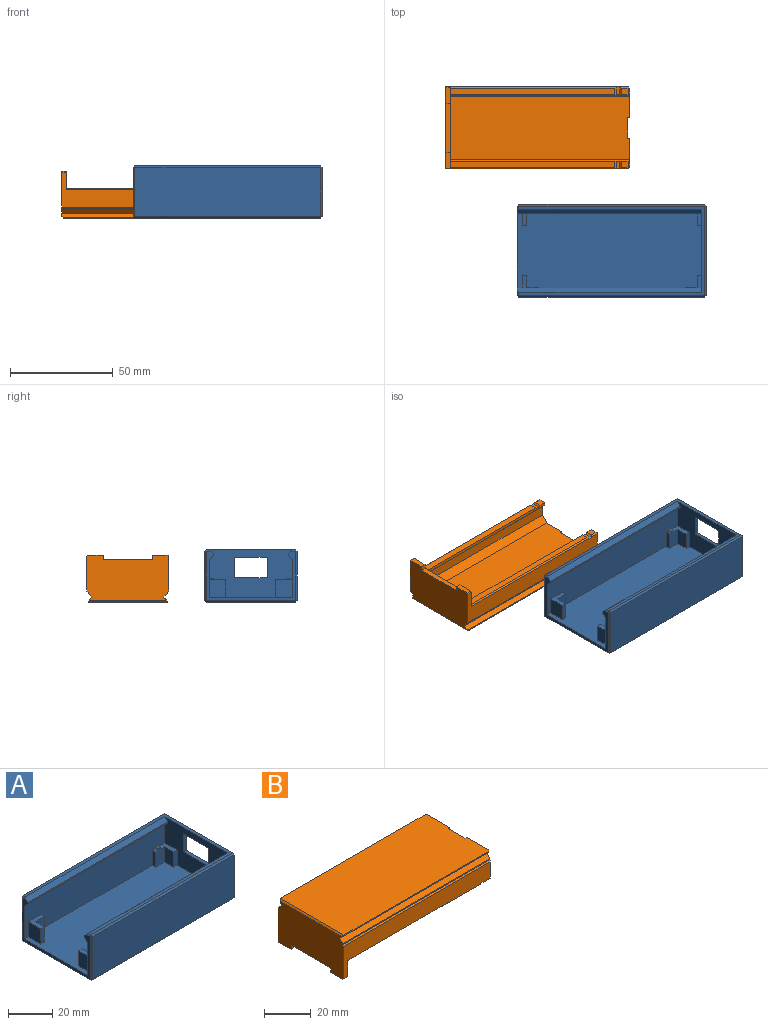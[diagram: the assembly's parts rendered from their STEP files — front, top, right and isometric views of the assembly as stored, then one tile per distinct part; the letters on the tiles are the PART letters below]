
ASSEMBLY  parts=2 mates=1
PART A: 75 faces, bbox 92.1x45.1x25.4 mm
  f0: plane 8x4mm, normal (0,0,1), area 21.6mm2, adj f1,f4,f29,f30,f32,f72
  f1: plane 89.7x18.2mm, normal (0,1,0), area 1496.4mm2, adj f0,f4,f6,f8,f15,f16,f17,f31
  f2: plane 2.2x1.08mm, normal (0,0,1), area 2.4mm2, adj f3,f24,f27,f70
  f3: plane 89.7x18.2mm, normal (0,-1,0), area 1496.4mm2, adj f2,f4,f6,f8,f18,f19,f23,f27
  f4: plane 40.3x23mm, normal (-1,0,0), area 621.3mm2, adj f0,f1,f3,f6,f11,f26,f28,f32
  f5: plane 43.5x23.8mm, normal (1,0,0), area 831.1mm2, adj f49,f50,f57,f58,f65,f66,f67,f68
  f6: plane 89.7x40.3mm, normal (0,0,1), area 3493.5mm2, adj f1,f3,f4,f8,f12,f13,f14,f15
  f7: plane 90.5x23.8mm, normal (0,1,0), area 2153.9mm2, adj f56,f57,f61,f62
  f8: plane 43.5x23.8mm, normal (-1,0,0), area 151.2mm2, adj f1,f3,f6,f34,f35,f36,f37,f38
  f9: plane 90.5x23.8mm, normal (0,-1,0), area 2153.9mm2, adj f47,f48,f50,f51
  f10: plane 90.5x43.5mm, normal (0,0,-1), area 3936.7mm2, adj f48,f49,f55,f56
  f11: plane 90.5x43.5mm, normal (0,0,1), area 354.1mm2, adj f4,f36,f37,f45,f51,f58,f62,f64
  f12: plane 8.4x5.8mm, normal (0,1,0), area 48.7mm2, adj f6,f13,f16,f17
  f13: plane 8.4x5.8mm, normal (1,0,0), area 48.7mm2, adj f6,f12,f14,f17
  f14: plane 8.4x2.2mm, normal (0,1,0), area 18.5mm2, adj f6,f13,f15,f17
  f15: plane 8.4x8mm, normal (-1,0,0), area 67.2mm2, adj f1,f6,f14,f17
  f16: plane 8.4x2.2mm, normal (1,0,0), area 18.5mm2, adj f1,f6,f12,f17
  f17: plane 8x8mm, normal (0,0,1), area 30.4mm2, adj f1,f12,f13,f14,f15,f16
  f18: plane 8.4x2.2mm, normal (1,0,0), area 18.5mm2, adj f3,f6,f22,f23
  f19: plane 8.4x8mm, normal (-1,0,0), area 67.2mm2, adj f3,f6,f20,f23
  f20: plane 8.4x2.2mm, normal (0,-1,0), area 18.5mm2, adj f6,f19,f21,f23
  f21: plane 8.4x5.8mm, normal (1,0,0), area 48.7mm2, adj f6,f20,f22,f23
  f22: plane 8.4x5.8mm, normal (0,-1,0), area 48.7mm2, adj f6,f18,f21,f23
  f23: plane 8x8mm, normal (0,0,1), area 30.4mm2, adj f3,f18,f19,f20,f21,f22
  f24: plane 9.2x5.8mm, normal (0,-1,0), area 50.4mm2, adj f2,f6,f25,f27,f28,f69,f70,f71
  f25: plane 8.4x5.8mm, normal (-1,0,0), area 48.7mm2, adj f6,f24,f26,f28
  f26: plane 8.4x2.2mm, normal (0,-1,0), area 18.5mm2, adj f4,f6,f25,f28
  f27: plane 8.4x2.2mm, normal (-1,0,0), area 18.5mm2, adj f2,f3,f6,f24
  f28: plane 8x4mm, normal (0,0,1), area 21.6mm2, adj f3,f4,f24,f25,f26,f71
  f29: plane 8.4x5.8mm, normal (-1,0,0), area 48.7mm2, adj f0,f6,f30,f32
  f30: plane 9.2x5.8mm, normal (0,1,0), area 50.4mm2, adj f0,f6,f29,f31,f33,f72,f73,f74
  f31: plane 8.4x2.2mm, normal (-1,0,0), area 18.5mm2, adj f1,f6,f30,f33
  f32: plane 8.4x2.2mm, normal (0,1,0), area 18.5mm2, adj f0,f4,f6,f29
  f33: plane 2.2x1.08mm, normal (0,0,1), area 2.4mm2, adj f1,f30,f31,f74
  f34: plane 89.7x0.8mm, normal (0,-1,0), area 71.8mm2, adj f4,f8,f35,f36
  f35: plane 89.7x2mm, normal (0,-0.71,-0.71), area 253.7mm2, adj f3,f4,f8,f34
  f36: plane 89.7x2mm, normal (0,-0.71,0.71), area 253.3mm2, adj f4,f8,f11,f34,f64
  f37: plane 89.7x2mm, normal (0,0.71,0.71), area 253.3mm2, adj f4,f8,f11,f38,f45
  f38: plane 89.7x0.8mm, normal (0,1,0), area 71.8mm2, adj f4,f8,f37,f39
  f39: plane 89.7x2mm, normal (0,0.71,-0.71), area 253.7mm2, adj f1,f4,f8,f38
  f40: plane 16x1.6mm, normal (0,0,-1), area 25.6mm2, adj f4,f41,f43,f66
  f41: plane 10x1.6mm, normal (0,1,0), area 16mm2, adj f4,f40,f42,f65
  f42: plane 16x1.6mm, normal (0,0,1), area 25.6mm2, adj f4,f41,f43,f67
  f43: plane 10x1.6mm, normal (0,-1,0), area 16mm2, adj f4,f40,f42,f68
  f44: plane 0.8x0.8mm, normal (0.58,-0.58,-0.58), area 0.6mm2, adj f48,f49,f50
  f45: plane 2.4x0.8mm, normal (-0.71,0,0.71), area 2.3mm2, adj f8,f11,f37,f46
  f46: plane 0.8x0.8mm, normal (-0.58,-0.58,0.58), area 0.6mm2, adj f45,f47,f51
  f47: plane 23.8x0.8mm, normal (-0.71,-0.71,0), area 26.9mm2, adj f8,f9,f46,f52
  f48: plane 90.5x0.8mm, normal (0,-0.71,-0.71), area 102.4mm2, adj f9,f10,f44,f52
  f49: plane 43.5x0.8mm, normal (0.71,0,-0.71), area 49.2mm2, adj f5,f10,f44,f53
  f50: plane 23.8x0.8mm, normal (0.71,-0.71,0), area 26.9mm2, adj f5,f9,f44,f54
  f51: plane 90.5x0.8mm, normal (0,-0.71,0.71), area 102.4mm2, adj f9,f11,f46,f54
  f52: plane 0.8x0.8mm, normal (-0.58,-0.58,-0.58), area 0.6mm2, adj f47,f48,f55
  f53: plane 0.8x0.8mm, normal (0.58,0.58,-0.58), area 0.6mm2, adj f49,f56,f57
  f54: plane 0.8x0.8mm, normal (0.58,-0.58,0.58), area 0.6mm2, adj f50,f51,f58
  f55: plane 43.5x0.8mm, normal (-0.71,0,-0.71), area 49.2mm2, adj f8,f10,f52,f59
  f56: plane 90.5x0.8mm, normal (0,0.71,-0.71), area 102.4mm2, adj f7,f10,f53,f59
  f57: plane 23.8x0.8mm, normal (0.71,0.71,0), area 26.9mm2, adj f5,f7,f53,f60
  f58: plane 43.5x0.8mm, normal (0.71,0,0.71), area 49.2mm2, adj f5,f11,f54,f60
  f59: plane 0.8x0.8mm, normal (-0.58,0.58,-0.58), area 0.6mm2, adj f55,f56,f61
  f60: plane 0.8x0.8mm, normal (0.58,0.58,0.58), area 0.6mm2, adj f57,f58,f62
  f61: plane 23.8x0.8mm, normal (-0.71,0.71,0), area 26.9mm2, adj f7,f8,f59,f63
  f62: plane 90.5x0.8mm, normal (0,0.71,0.71), area 102.4mm2, adj f7,f11,f60,f63
  f63: plane 0.8x0.8mm, normal (-0.58,0.58,0.58), area 0.6mm2, adj f61,f62,f64
  f64: plane 2.4x0.8mm, normal (-0.71,0,0.71), area 2.3mm2, adj f8,f11,f36,f63
  f65: plane 11.6x0.8mm, normal (0.71,0.71,0), area 12.2mm2, adj f5,f41,f66,f67
  f66: plane 17.6x0.8mm, normal (0.71,0,-0.71), area 19mm2, adj f5,f40,f65,f68
  f67: plane 17.6x0.8mm, normal (0.71,0,0.71), area 19mm2, adj f5,f42,f65,f68
  f68: plane 11.6x0.8mm, normal (0.71,-0.71,0), area 12.2mm2, adj f5,f43,f66,f67
  f69: plane 2.2x1.32mm, normal (0,0,1), area 2.9mm2, adj f3,f24,f70,f71
  f70: plane 2.2x0.8mm, normal (-0.71,0,0.71), area 2.5mm2, adj f2,f3,f24,f69
  f71: plane 2.2x0.8mm, normal (0.71,0,0.71), area 2.5mm2, adj f3,f24,f28,f69
  f72: plane 2.2x0.8mm, normal (0.71,0,0.71), area 2.5mm2, adj f0,f1,f30,f73
  f73: plane 2.2x1.32mm, normal (0,0,1), area 2.9mm2, adj f1,f30,f72,f74
  f74: plane 2.2x0.8mm, normal (-0.71,0,0.71), area 2.5mm2, adj f1,f30,f33,f73
PART B: 63 faces, bbox 89.6x39.9x22.8 mm
  f0: plane 80x3.2mm, normal (0,0,-1), area 256mm2, adj f3,f7,f13,f57
  f1: plane 3.2x3.2mm, normal (0,0,-1), area 10.2mm2, adj f4,f6,f41,f62
  f2: plane 89x17mm, normal (0,1,0), area 785.2mm2, adj f7,f8,f9,f13,f42,f43,f45,f52
  f3: plane 86.4x1.6mm, normal (0,-1,0), area 136.3mm2, adj f0,f13,f29,f30,f44,f57,f58,f59
  f4: plane 86.4x1.6mm, normal (0,1,0), area 136.3mm2, adj f1,f13,f31,f32,f39,f60,f61,f62
  f5: plane 80.6x0.6mm, normal (0,-0.71,-0.71), area 68.1mm2, adj f13,f26,f31,f60
  f6: plane 3.8x0.6mm, normal (0,-0.71,-0.71), area 3mm2, adj f1,f26,f40,f62
  f7: plane 80.6x0.6mm, normal (0,0.71,-0.71), area 68.1mm2, adj f0,f2,f13,f57
  f8: plane 3.8x0.6mm, normal (0,0.71,-0.71), area 3mm2, adj f2,f30,f45,f58
  f9: plane 39.9x22mm, normal (-1,0,0), area 812.4mm2, adj f2,f10,f14,f15,f19,f20,f21,f24
  f10: plane 7.55x2.4mm, normal (0,0,-1), area 18.1mm2, adj f9,f13,f51,f55
  f11: plane 87.2x30.7mm, normal (0,0,-1), area 2667mm2, adj f12,f13,f22,f23,f25,f34,f35,f36
  f12: plane 14.35x13.8mm, normal (1,0,0), area 48.2mm2, adj f11,f17,f19,f20,f21,f22,f32,f33
  f13: plane 39.9x20.4mm, normal (1,0,0), area 703.5mm2, adj f0,f2,f3,f4,f5,f7,f10,f11
  f14: plane 89.6x1.88mm, normal (0,0.71,0.71), area 238.6mm2, adj f9,f15,f24,f25
  f15: plane 89.6x1.88mm, normal (0,0.71,-0.71), area 237.7mm2, adj f9,f14,f16,f25,f47,f49
  f16: plane 88x0.52mm, normal (0,1,0), area 45.5mm2, adj f15,f17,f47,f49
  f17: plane 88.8x38.7mm, normal (0,0,1), area 3425.9mm2, adj f12,f16,f18,f25,f34,f35,f36,f49
  f18: plane 88x0.52mm, normal (0,-1,0), area 45.5mm2, adj f17,f19,f48,f50
  f19: plane 89.6x1.88mm, normal (0,-0.71,-0.71), area 237.7mm2, adj f9,f12,f18,f20,f48,f50
  f20: plane 89.6x1.88mm, normal (0,-0.71,0.71), area 238.6mm2, adj f9,f12,f19,f21
  f21: plane 89.6x0.52mm, normal (0,-1,0), area 46.3mm2, adj f9,f12,f20,f37
  f22: plane 87.2x3.2mm, normal (0,0.71,-0.71), area 394.6mm2, adj f11,f12,f13,f33
  f23: plane 87.2x3.2mm, normal (0,-0.71,-0.71), area 394.6mm2, adj f11,f13,f25,f28
  f24: plane 89.6x0.52mm, normal (0,1,0), area 46.3mm2, adj f9,f14,f25,f42
  f25: plane 14.35x13.8mm, normal (1,0,0), area 48.2mm2, adj f11,f14,f15,f17,f23,f24,f28,f29
  f26: plane 89x17mm, normal (0,-1,0), area 785.2mm2, adj f5,f6,f9,f13,f37,f38,f40,f51
  f27: plane 7.55x2.4mm, normal (0,0,-1), area 18.1mm2, adj f9,f13,f52,f53
  f28: plane 87.2x5mm, normal (0,-1,0), area 436mm2, adj f13,f23,f25,f29
  f29: plane 87.2x2.4mm, normal (0,-0.71,0.71), area 295.5mm2, adj f3,f13,f25,f28,f44
  f30: plane 3.2x3.2mm, normal (0,0,-1), area 10.2mm2, adj f3,f8,f46,f58
  f31: plane 80x3.2mm, normal (0,0,-1), area 256mm2, adj f4,f5,f13,f60
  f32: plane 87.2x2.4mm, normal (0,0.71,0.71), area 295.5mm2, adj f4,f12,f13,f33,f39
  f33: plane 87.2x5mm, normal (0,1,0), area 436mm2, adj f12,f13,f22,f32
  f34: plane 2.4x1mm, normal (0,-1,0), area 2.4mm2, adj f11,f17,f25,f35
  f35: plane 10x2.4mm, normal (1,0,0), area 24mm2, adj f11,f17,f34,f36
  f36: plane 2.4x1mm, normal (0,1,0), area 2.4mm2, adj f11,f12,f17,f35
  f37: plane 89.6x0.6mm, normal (0,-0.71,0.71), area 75.8mm2, adj f9,f21,f26,f38
  f38: plane 9x0.6mm, normal (0.71,-0.71,0), area 7.4mm2, adj f12,f26,f37,f40
  f39: plane 2.4x0.8mm, normal (0.71,0.71,0), area 1.8mm2, adj f4,f12,f32,f41
  f40: plane 0.8x0.8mm, normal (0.58,-0.58,-0.58), area 0.5mm2, adj f6,f26,f38,f41
  f41: plane 3.2x0.8mm, normal (0.71,0,-0.71), area 3.2mm2, adj f1,f12,f39,f40
  f42: plane 89.6x0.6mm, normal (0,0.71,0.71), area 75.8mm2, adj f2,f9,f24,f43
  f43: plane 9x0.6mm, normal (0.71,0.71,0), area 7.4mm2, adj f2,f25,f42,f45
  f44: plane 2.4x0.8mm, normal (0.71,-0.71,0), area 1.8mm2, adj f3,f25,f29,f46
  f45: plane 0.8x0.8mm, normal (0.58,0.58,-0.58), area 0.5mm2, adj f2,f8,f43,f46
  f46: plane 3.2x0.8mm, normal (0.71,0,-0.71), area 3.2mm2, adj f25,f30,f44,f45
  f47: plane 1.32x0.8mm, normal (-0.71,0.71,0), area 0.6mm2, adj f9,f15,f16,f56
  f48: plane 1.32x0.8mm, normal (-0.71,-0.71,0), area 0.6mm2, adj f9,f18,f19,f56
  f49: plane 1.32x0.8mm, normal (0.71,0.71,0), area 1mm2, adj f15,f16,f17,f25
  f50: plane 1.32x0.8mm, normal (0.71,-0.71,0), area 1mm2, adj f12,f17,f18,f19
  f51: plane 2.4x0.4mm, normal (0,-0.71,-0.71), area 1.4mm2, adj f9,f10,f13,f26
  f52: plane 2.4x0.4mm, normal (0,0.71,-0.71), area 1.4mm2, adj f2,f9,f13,f27
  f53: plane 2.4x2.2mm, normal (0,-1,0), area 5.3mm2, adj f9,f13,f27,f54
  f54: plane 24x2.4mm, normal (0,0,-1), area 57.6mm2, adj f9,f13,f53,f55
  f55: plane 2.4x2.2mm, normal (0,1,0), area 5.3mm2, adj f9,f10,f13,f54
  f56: plane 38.7x0.8mm, normal (-0.71,0,0.71), area 42.9mm2, adj f9,f17,f47,f48
  f57: plane 3.8x0.8mm, normal (0.71,0,-0.71), area 4mm2, adj f0,f2,f3,f7,f59
  f58: plane 3.8x0.8mm, normal (-0.71,0,-0.71), area 4mm2, adj f2,f3,f8,f30,f59
  f59: plane 3.8x1.6mm, normal (0,0,-1), area 6.1mm2, adj f2,f3,f57,f58
  f60: plane 3.8x0.8mm, normal (0.71,0,-0.71), area 4mm2, adj f4,f5,f26,f31,f61
  f61: plane 3.8x1.6mm, normal (0,0,-1), area 6.1mm2, adj f4,f26,f60,f62
  f62: plane 3.8x0.8mm, normal (-0.71,0,-0.71), area 4mm2, adj f1,f4,f6,f26,f61
PLACE A t=(12.36,-30.78,0.35)mm
PLACE B rot(axis=(1,0,0),180deg) t=(81.44,29.03,20.95)mm
MATE planar B.f17 <-> A.f10  axis (0,0,-1) through (-23.5,29.03,-2.05)mm
